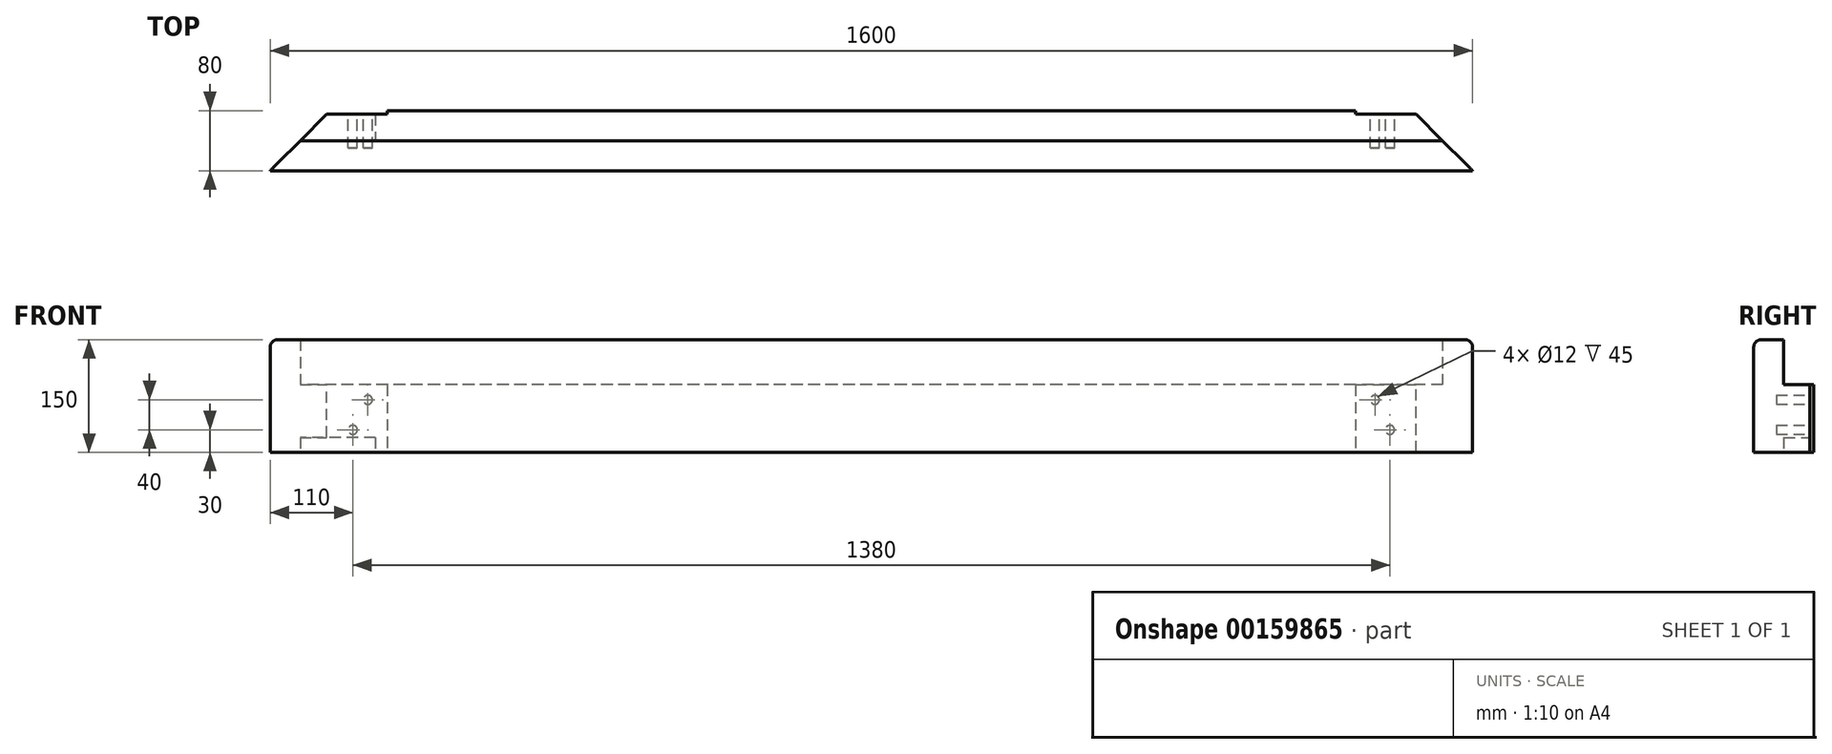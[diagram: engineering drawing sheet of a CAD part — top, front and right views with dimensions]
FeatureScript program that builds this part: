
annotation { "Feature Type Name" : "Feature", "Feature Type Description" : "" }
export const myFeature = defineFeature(function(context is Context, id is Id, definition is map)
    precondition{}
    {
        {
            assignVariable(context, id + "F0", {"name" : "L", "anyValue" : 1700 * mm - 100 * mm});
        }
        {
            assignVariable(context, id + "F1", {"name" : "B", "anyValue" : 80 * mm});
        }
        {
            var Q0;
            Q0=qCreatedBy(makeId("Right.planeOp"),FACE);
            var sketch = newSketch(context, id + "F2", { "sketchPlane" : qUnion([Q0])});
            skLineSegment(sketch, "E0.bottom", {"start": v(-40, -75) * mm, "end": v(40, -75) * mm});
            skLineSegment(sketch, "E0.top", {"start": v(-40, 75) * mm, "end": v(0, 75) * mm});
            skLineSegment(sketch, "E0.left", {"start": v(-40, -75) * mm, "end": v(-40, 75) * mm});
            skLineSegment(sketch, "E0.right", {"start": v(40, -75) * mm, "end": v(40, 15) * mm});
            skPoint(sketch, "E0.middle", {"position": v(0, 0) * mm});
            skLineSegment(sketch, "E1", {"start": v(0, 75) * mm, "end": v(0, 15) * mm});
            skLineSegment(sketch, "E2", {"start": v(0, 15) * mm, "end": v(40, 15) * mm});
            skSolve(sketch);
        }
        {
            var Q0;
            Q0 = qSketchRegion(id + "F2", true);
            extrude(context, id + "F3", {"entities" : qUnion([Q0]), "endBound" : BoundingType.SYMMETRIC, "depth" : getVariable(context, 'L')});
        }
        {
            var Q0;
            Q0=makeQuery(id+"F3.opExtrude","CAP_EDGE",EDGE,{"disambiguationData":[OSD([sQuery(id+"F2.wireOp",EDGE,"E0.right")])],"isStart":false});
            var Q1;
            Q1=makeQuery(id+"F3.opExtrude","CAP_EDGE",EDGE,{"disambiguationData":[OSD([sQuery(id+"F2.wireOp",EDGE,"E0.right")])],"isStart":true});
            chamfer(context, id + "F4", {"entities" : qUnion([Q0, Q1]), "width" : getVariable(context, 'B'), "tangentPropagation" : true});
        }
        {
            var Q0;
            Q0=makeQuery(id+"F3.opExtrude","SWEPT_FACE",FACE,{"disambiguationData":[OSD([sQuery(id+"F2.wireOp",EDGE,"E0.right")])]});
            var sketch = newSketch(context, id + "F5", { "sketchPlane" : qUnion([Q0])});
            skCircle(sketch, "E3", {"center": v(-690, -45) * mm, "radius": 6 * mm});
            skCircle(sketch, "E4", {"center": v(-670, -5) * mm, "radius": 6 * mm});
            skCircle(sketch, "E5.MirrorC", {"center": v(670, -5) * mm, "radius": 6 * mm});
            skCircle(sketch, "E6.MirrorC", {"center": v(690, -45) * mm, "radius": 6 * mm});
            skSolve(sketch);
        }
        {
            var Q0;
            Q0 = qSketchRegion(id + "F5", true);
            extrude(context, id + "F6", {"entities" : qUnion([Q0]), "operationType" : NewBodyOperationType.REMOVE, "oppositeDirection" : true, "depth" : getVariable(context, 'B') - 30 * mm});
        }
        {
            var Q0;
            Q0=makeQuery(id+"F3.opExtrude","SWEPT_FACE",FACE,{"disambiguationData":[OSD([sQuery(id+"F2.wireOp",EDGE,"E0.right")])]});
            var sketch = newSketch(context, id + "F7", { "sketchPlane" : qUnion([Q0])});
            skLineSegment(sketch, "E7.bottom", {"start": v(-644, 15) * mm, "end": v(-760, 15) * mm});
            skLineSegment(sketch, "E7.top", {"start": v(-644, -75) * mm, "end": v(-760, -75) * mm});
            skLineSegment(sketch, "E7.left", {"start": v(-644, 15) * mm, "end": v(-644, -75) * mm});
            skLineSegment(sketch, "E7.right", {"start": v(-760, 15) * mm, "end": v(-760, -75) * mm});
            skLineSegment(sketch, "E8.MirrorCS", {"start": v(760, 15) * mm, "end": v(760, -75) * mm});
            skLineSegment(sketch, "E9.MirrorCS", {"start": v(644, 15) * mm, "end": v(760, 15) * mm});
            skLineSegment(sketch, "E10.MirrorCS", {"start": v(644, 15) * mm, "end": v(644, -75) * mm});
            skLineSegment(sketch, "E11.MirrorCS", {"start": v(644, -75) * mm, "end": v(760, -75) * mm});
            skSolve(sketch);
        }
        {
            var Q0;
            Q0 = qSketchRegion(id + "F7", true);
            extrude(context, id + "F8", {"entities" : qUnion([Q0]), "operationType" : NewBodyOperationType.REMOVE, "oppositeDirection" : true, "depth" : 5 * mm});
        }
        {
            var Q0;
            Q0=makeQuery(id+"F3.opExtrude","SWEPT_EDGE",EDGE,{"disambiguationData":[OSD([sQuery(id+"F2.wireOp",EDGE,"E0.top"),sQuery(id+"F2.wireOp",EDGE,"E0.left")])]});
            fillet(context, id + "F9", {"entities" : qUnion([Q0]), "radius" : 10 * mm, "tangentPropagation" : true, "allowEdgeOverflow" : false});
        }
        {
            var Q0;
            Q0=makeQuery(id+"F3.opExtrude","SWEPT_FACE",FACE,{"disambiguationData":[OSD([sQuery(id+"F2.wireOp",EDGE,"E0.bottom")])]});
            var sketch = newSketch(context, id + "F10", { "sketchPlane" : qUnion([Q0])});
            skLineSegment(sketch, "E12.bottom", {"start": v(-660, -100) * mm, "end": v(-760, -100) * mm});
            skLineSegment(sketch, "E12.top", {"start": v(-660, 0) * mm, "end": v(-760, 0) * mm});
            skLineSegment(sketch, "E12.left", {"start": v(-660, -100) * mm, "end": v(-660, 0) * mm});
            skLineSegment(sketch, "E12.right", {"start": v(-760, -100) * mm, "end": v(-760, 0) * mm});
            skLineSegment(sketch, "E13", {"start": v(-660, -50) * mm, "end": v(-760, -50) * mm, "construction": true});
            skSolve(sketch);
        }
        {
            var Q0;
            Q0 = qSketchRegion(id + "F10", true);
            extrude(context, id + "F11", {"entities" : qUnion([Q0]), "operationType" : NewBodyOperationType.REMOVE, "oppositeDirection" : true, "depth" : 20 * mm});
        }
    });
